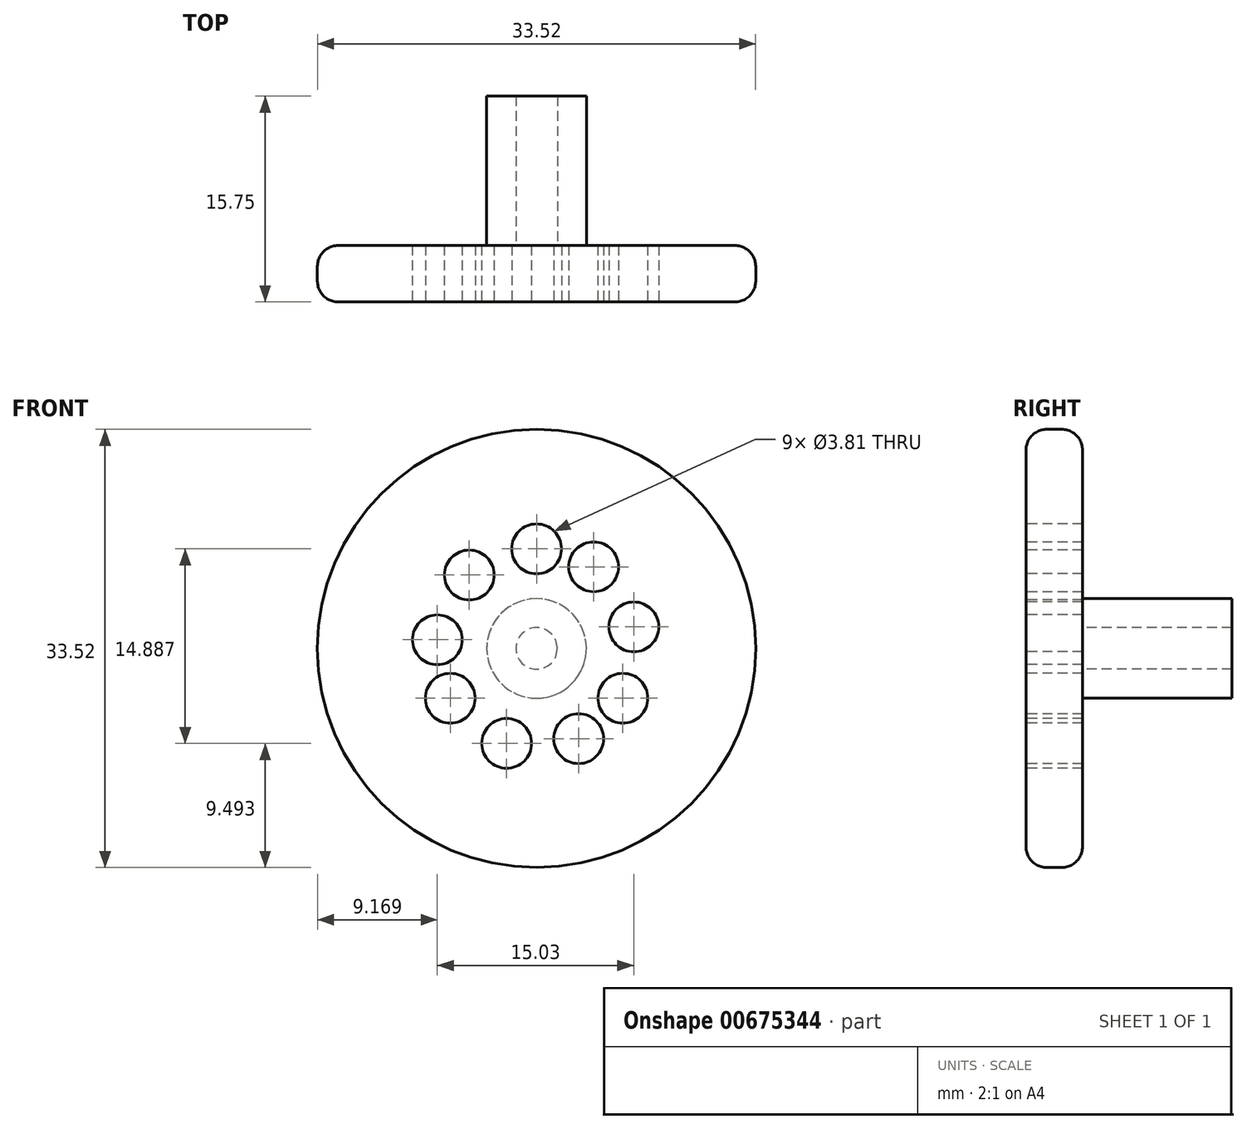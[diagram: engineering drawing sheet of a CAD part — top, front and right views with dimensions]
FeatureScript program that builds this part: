
annotation { "Feature Type Name" : "Feature", "Feature Type Description" : "" }
export const myFeature = defineFeature(function(context is Context, id is Id, definition is map)
    precondition{}
    {
        {
            var Q0;
            Q0=qCreatedBy(makeId("Front.planeOp"),FACE);
            var sketch = newSketch(context, id + "F0", { "sketchPlane" : qUnion([Q0])});
            skLineSegment(sketch, "E0", {"start": v(0, 0) * mm, "end": v(16.76, 0) * mm});
            skCircle(sketch, "E1", {"center": v(0, 0) * mm, "radius": 16.76 * mm});
            skSolve(sketch);
        }
        {
            var Q0;
            Q0=makeQuery(id+"F0.imprint","IMPRINT",FACE,{"disambiguationData":[TD([[makeQuery(id+"F0.imprint","IMPRINT",EDGE,{"derivedFrom":sQuery(id+"F0.wireOp",EDGE,"E1")}),1.0]])]});
            extrude(context, id + "F1", {"entities" : qUnion([Q0]), "depth" : 4.32 * mm, "offsetDistance" : 25.4 * mm});
        }
        {
            var Q0;
            Q0=makeQuery(id+"F1.opExtrude","CAP_FACE",FACE,{"disambiguationData":[OSD([sQuery(id+"F0.wireOp",EDGE,"E1")])],"isStart":true});
            var Q1;
            Q1=makeQuery(id+"F1.opExtrude","CAP_EDGE",EDGE,{"disambiguationData":[OSD([sQuery(id+"F0.wireOp",EDGE,"E1")])],"isStart":false});
            fillet(context, id + "F2", {"entities" : qUnion([Q0, Q1]), "radius" : 1.59 * mm, "tangentPropagation" : true, "allowEdgeOverflow" : false});
        }
        {
            var Q0;
            Q0=makeQuery(id+"F1.opExtrude","CAP_FACE",FACE,{"disambiguationData":[OSD([sQuery(id+"F0.wireOp",EDGE,"E1")])],"isStart":false});
            var sketch = newSketch(context, id + "F3", { "sketchPlane" : qUnion([Q0])});
            skLineSegment(sketch, "E2", {"start": v(0, 0) * mm, "end": v(0, 7.62) * mm});
            skCircle(sketch, "E3", {"center": v(0, 7.62) * mm, "radius": 1.9 * mm});
            skCircle(sketch, "E4.1.0", {"center": v(-6.6, -3.8) * mm, "radius": 1.9 * mm});
            skCircle(sketch, "E4.2.0", {"center": v(6.6, -3.81) * mm, "radius": 1.9 * mm});
            skPoint(sketch, "E4.center", {"position": v(0, 0) * mm});
            skCircle(sketch, "E5.1.0", {"center": v(7.44, 1.65) * mm, "radius": 1.9 * mm});
            skCircle(sketch, "E5.1.1", {"center": v(-2.3, -7.27) * mm, "radius": 1.9 * mm});
            skCircle(sketch, "E5.1.2", {"center": v(-5.15, 5.62) * mm, "radius": 1.9 * mm});
            skCircle(sketch, "E5.2.0", {"center": v(3.22, -6.9) * mm, "radius": 1.9 * mm});
            skCircle(sketch, "E5.2.1", {"center": v(-7.6, 0.66) * mm, "radius": 1.9 * mm});
            skCircle(sketch, "E5.2.2", {"center": v(4.37, 6.24) * mm, "radius": 1.9 * mm});
            skLineSegment(sketch, "E5.anchor1", {"start": v(0, 0) * mm, "end": v(0, 7.62) * mm, "construction": true});
            skLineSegment(sketch, "E5.anchor2", {"start": v(0, 0) * mm, "end": v(3.22, -6.9) * mm, "construction": true});
            skSolve(sketch);
        }
        {
            var Q0;
            Q0=makeQuery(id+"F3.imprint","IMPRINT",FACE,{"disambiguationData":[TD([[makeQuery(id+"F3.imprint","IMPRINT",EDGE,{"derivedFrom":sQuery(id+"F3.wireOp",EDGE,"E3")}),1.0]])]});
            var Q1;
            Q1=makeQuery(id+"F3.imprint","IMPRINT",FACE,{"disambiguationData":[TD([[makeQuery(id+"F3.imprint","IMPRINT",EDGE,{"derivedFrom":sQuery(id+"F3.wireOp",EDGE,"E5.2.2")}),1.0]])]});
            var Q2;
            Q2=makeQuery(id+"F3.imprint","IMPRINT",FACE,{"disambiguationData":[TD([[makeQuery(id+"F3.imprint","IMPRINT",EDGE,{"derivedFrom":sQuery(id+"F3.wireOp",EDGE,"E5.1.0")}),1.0]])]});
            var Q3;
            Q3=makeQuery(id+"F3.imprint","IMPRINT",FACE,{"disambiguationData":[TD([[makeQuery(id+"F3.imprint","IMPRINT",EDGE,{"derivedFrom":sQuery(id+"F3.wireOp",EDGE,"E4.2.0")}),1.0]])]});
            var Q4;
            Q4=makeQuery(id+"F3.imprint","IMPRINT",FACE,{"disambiguationData":[TD([[makeQuery(id+"F3.imprint","IMPRINT",EDGE,{"derivedFrom":sQuery(id+"F3.wireOp",EDGE,"E5.2.0")}),1.0]])]});
            var Q5;
            Q5=makeQuery(id+"F3.imprint","IMPRINT",FACE,{"disambiguationData":[TD([[makeQuery(id+"F3.imprint","IMPRINT",EDGE,{"derivedFrom":sQuery(id+"F3.wireOp",EDGE,"E5.1.1")}),1.0]])]});
            var Q6;
            Q6=makeQuery(id+"F3.imprint","IMPRINT",FACE,{"disambiguationData":[TD([[makeQuery(id+"F3.imprint","IMPRINT",EDGE,{"derivedFrom":sQuery(id+"F3.wireOp",EDGE,"E4.1.0")}),1.0]])]});
            var Q7;
            Q7=makeQuery(id+"F3.imprint","IMPRINT",FACE,{"disambiguationData":[TD([[makeQuery(id+"F3.imprint","IMPRINT",EDGE,{"derivedFrom":sQuery(id+"F3.wireOp",EDGE,"E5.2.1")}),1.0]])]});
            var Q8;
            Q8=makeQuery(id+"F3.imprint","IMPRINT",FACE,{"disambiguationData":[TD([[makeQuery(id+"F3.imprint","IMPRINT",EDGE,{"derivedFrom":sQuery(id+"F3.wireOp",EDGE,"E5.1.2")}),1.0]])]});
            extrude(context, id + "F4", {"entities" : qUnion([Q0, Q1, Q2, Q3, Q4, Q5, Q6, Q7, Q8]), "operationType" : NewBodyOperationType.REMOVE, "oppositeDirection" : true, "depth" : 25.4 * mm, "offsetDistance" : 25.4 * mm});
        }
        {
            var Q0;
            Q0=makeQuery(id+"F1.opExtrude","CAP_FACE",FACE,{"disambiguationData":[OSD([sQuery(id+"F0.wireOp",EDGE,"E1")])],"isStart":true});
            var sketch = newSketch(context, id + "F5", { "sketchPlane" : qUnion([Q0])});
            skCircle(sketch, "E6", {"center": v(0, 0) * mm, "radius": 1.59 * mm});
            skCircle(sketch, "E7", {"center": v(0, 0) * mm, "radius": 3.81 * mm});
            skSolve(sketch);
        }
        {
            var Q0;
            Q0=makeQuery(id+"F5.imprint","IMPRINT",FACE,{"disambiguationData":[TD([[makeQuery(id+"F5.imprint","IMPRINT",EDGE,{"derivedFrom":sQuery(id+"F5.wireOp",EDGE,"E6")}),1.0]])]});
            extrude(context, id + "F6", {"entities" : qUnion([Q0]), "operationType" : NewBodyOperationType.REMOVE, "depth" : 19.05 * mm, "offsetDistance" : 25.4 * mm});
        }
        {
            var Q0;
            Q0 = qSketchRegion(id + "F5", true);
            extrude(context, id + "F7", {"entities" : qUnion([Q0]), "operationType" : NewBodyOperationType.ADD, "depth" : 11.43 * mm, "offsetDistance" : 25.4 * mm});
        }
    });
